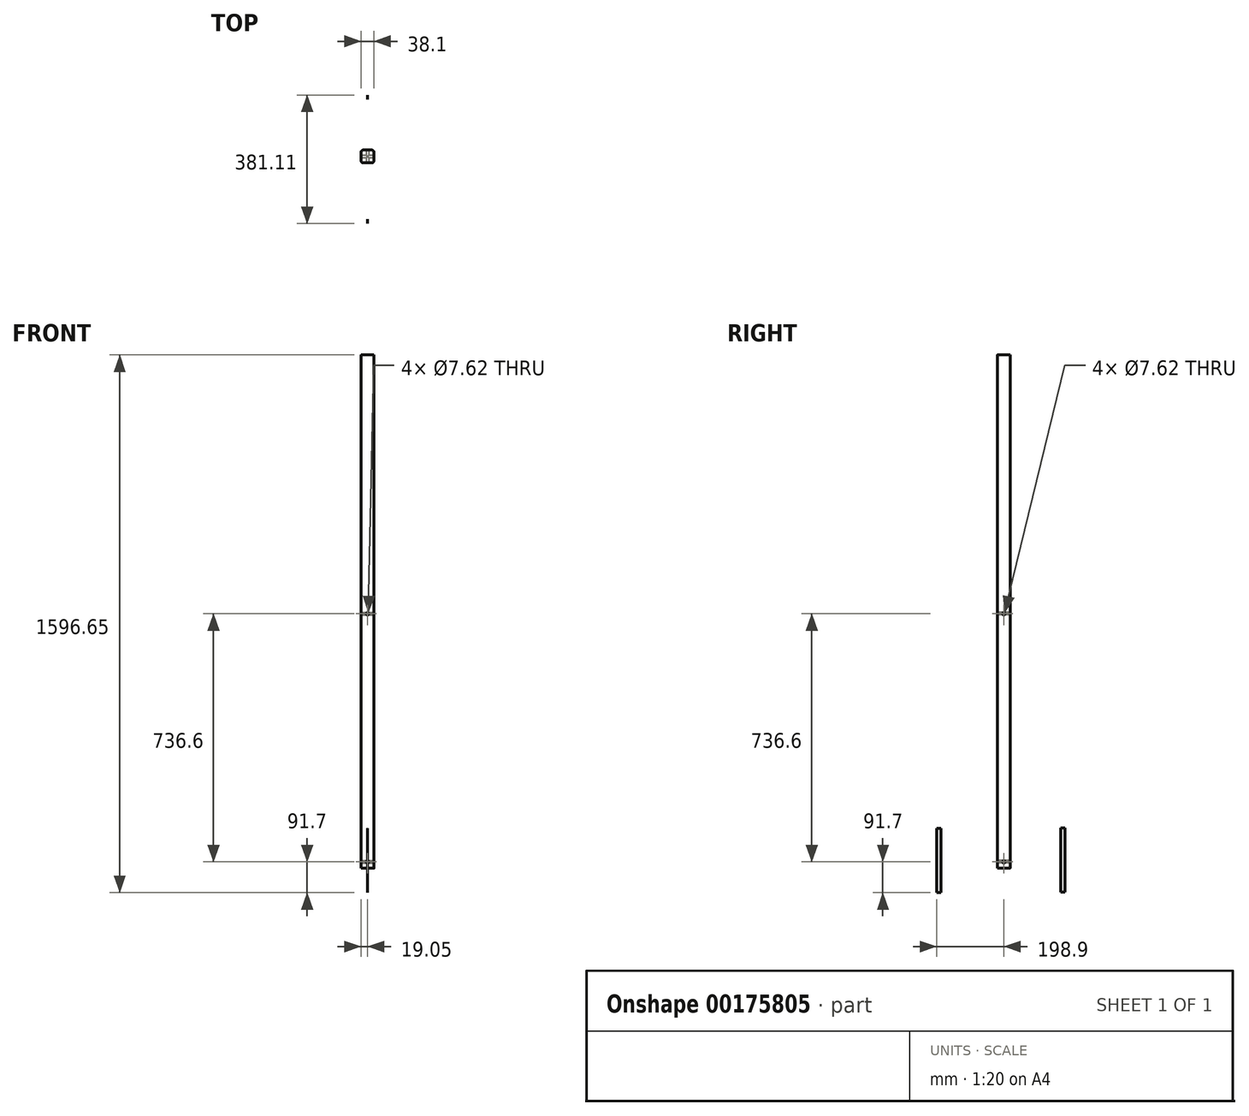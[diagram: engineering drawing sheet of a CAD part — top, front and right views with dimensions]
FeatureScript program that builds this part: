
annotation { "Feature Type Name" : "Feature", "Feature Type Description" : "" }
export const myFeature = defineFeature(function(context is Context, id is Id, definition is map)
    precondition{}
    {
        {
            var Q0;
            Q0=qCreatedBy(makeId("Top.planeOp"),FACE);
            var sketch = newSketch(context, id + "F0", { "sketchPlane" : qUnion([Q0])});
            skLineSegment(sketch, "E0.bottom", {"start": v(12.7, 19.05) * mm, "end": v(-12.7, 19.05) * mm});
            skLineSegment(sketch, "E0.top", {"start": v(12.7, -19.05) * mm, "end": v(-12.7, -19.05) * mm});
            skLineSegment(sketch, "E0.left", {"start": v(19.05, 12.7) * mm, "end": v(19.05, -12.7) * mm});
            skLineSegment(sketch, "E0.right", {"start": v(-19.05, 12.7) * mm, "end": v(-19.05, -12.7) * mm});
            skPoint(sketch, "E0.middle", {"position": v(0, 0) * mm});
            skPoint(sketch, "E1.visualSharp", {"position": v(-19.05, 19.05) * mm});
            skArc(sketch, "E1.filletArc", {"start": v(-12.7, 19.05) * mm, "mid": v(-17.2, 17.2) * mm, "end": v(-19.05, 12.7) * mm});
            skPoint(sketch, "E2.visualSharp", {"position": v(19.05, 19.05) * mm});
            skArc(sketch, "E2.filletArc", {"start": v(19.05, 12.7) * mm, "mid": v(17.2, 17.2) * mm, "end": v(12.7, 19.05) * mm});
            skPoint(sketch, "E3.visualSharp", {"position": v(19.05, -19.05) * mm});
            skArc(sketch, "E3.filletArc", {"start": v(12.7, -19.05) * mm, "mid": v(17.2, -17.2) * mm, "end": v(19.05, -12.7) * mm});
            skPoint(sketch, "E4.visualSharp", {"position": v(-19.05, -19.05) * mm});
            skArc(sketch, "E4.filletArc", {"start": v(-19.05, -12.7) * mm, "mid": v(-17.2, -17.2) * mm, "end": v(-12.7, -19.05) * mm});
            skSolve(sketch);
        }
        {
            var Q0;
            Q0=qSketchRegion(id+"F0",true);
            extrude(context, id + "F1", {"entities" : qUnion([Q0]), "depth" : 1524 * mm});
        }
        {
            var Q0;
            Q0=qCreatedBy(makeId("Right.planeOp"),FACE);
            var sketch = newSketch(context, id + "F2", { "sketchPlane" : qUnion([Q0])});
            skLineSegment(sketch, "E5.bottom", {"start": v(-186.2, -72.65) * mm, "end": v(-198.9, -72.65) * mm});
            skLineSegment(sketch, "E5.top", {"start": v(-186.2, 117.85) * mm, "end": v(-198.9, 117.85) * mm});
            skLineSegment(sketch, "E5.left", {"start": v(-186.2, -72.65) * mm, "end": v(-186.2, 117.85) * mm});
            skLineSegment(sketch, "E5.right", {"start": v(-198.9, -72.65) * mm, "end": v(-198.9, 117.85) * mm});
            skPoint(sketch, "E5.middle", {"position": v(-192.55, 22.6) * mm});
            skSolve(sketch);
        }
        {
            var Q0;
            Q0=qCreatedBy(makeId("Right.planeOp"),FACE);
            var sketch = newSketch(context, id + "F3", { "sketchPlane" : qUnion([Q0])});
            skLineSegment(sketch, "E6.bottom", {"start": v(182.21, -70.47) * mm, "end": v(169.51, -70.47) * mm});
            skLineSegment(sketch, "E6.top", {"start": v(182.21, 120.03) * mm, "end": v(169.51, 120.03) * mm});
            skLineSegment(sketch, "E6.left", {"start": v(182.21, -70.47) * mm, "end": v(182.21, 120.03) * mm});
            skLineSegment(sketch, "E6.right", {"start": v(169.51, -70.47) * mm, "end": v(169.51, 120.03) * mm});
            skPoint(sketch, "E6.middle", {"position": v(175.86, 24.78) * mm});
            skSolve(sketch);
        }
        {
            var Q0;
            Q0=makeQuery(id+"F2.imprint","IMPRINT",FACE,{"disambiguationData":[TD([[makeQuery(id+"F2.imprint","IMPRINT",EDGE,{"derivedFrom":sQuery(id+"F2.wireOp",EDGE,"E5.bottom")}),-1.0]])]});
            extrude(context, id + "F4", {"entities" : qUnion([Q0]), "depth" : 0.25 * mm});
        }
        {
            var Q0;
            Q0=makeQuery(id+"F3.imprint","IMPRINT",FACE,{"disambiguationData":[TD([[makeQuery(id+"F3.imprint","IMPRINT",EDGE,{"derivedFrom":sQuery(id+"F3.wireOp",EDGE,"E6.bottom")}),-1.0]])]});
            extrude(context, id + "F5", {"entities" : qUnion([Q0]), "depth" : 0.25 * mm});
        }
        {
            var Q0;
            Q0=makeQuery(id+"F1.opExtrude","SWEPT_FACE",FACE,{"disambiguationData":[OSD([sQuery(id+"F0.wireOp",EDGE,"E0.left")])]});
            var sketch = newSketch(context, id + "F6", { "sketchPlane" : qUnion([Q0])});
            skLineSegment(sketch, "E7", {"start": v(0, 0) * mm, "end": v(0, 755.65) * mm});
            skCircle(sketch, "E8", {"center": v(0, 755.65) * mm, "radius": 3.81 * mm});
            skSolve(sketch);
        }
        {
            var Q0;
            Q0 = qSketchRegion(id + "F6", true);
            extrude(context, id + "F7", {"entities" : qUnion([Q0]), "operationType" : NewBodyOperationType.REMOVE, "oppositeDirection" : true, "depth" : 38.1 * mm});
        }
        {
            var Q0;
            Q0=makeQuery(id+"F1.opExtrude","SWEPT_FACE",FACE,{"disambiguationData":[OSD([sQuery(id+"F0.wireOp",EDGE,"E0.top")])]});
            var sketch = newSketch(context, id + "F8", { "sketchPlane" : qUnion([Q0])});
            skLineSegment(sketch, "E9", {"start": v(0, 0) * mm, "end": v(0, 755.65) * mm});
            skCircle(sketch, "E10", {"center": v(0, 755.65) * mm, "radius": 3.81 * mm});
            skLineSegment(sketch, "E11", {"start": v(0, 0) * mm, "end": v(0, 19.05) * mm});
            skCircle(sketch, "E12", {"center": v(0, 19.05) * mm, "radius": 3.81 * mm});
            skSolve(sketch);
        }
        {
            var Q0;
            Q0 = qSketchRegion(id + "F8", true);
            extrude(context, id + "F9", {"entities" : qUnion([Q0]), "operationType" : NewBodyOperationType.REMOVE, "oppositeDirection" : true, "depth" : 38.1 * mm});
        }
        {
            var Q0;
            Q0 = qSketchRegion(id + "F8", true);
            extrude(context, id + "F10", {"entities" : qUnion([Q0]), "operationType" : NewBodyOperationType.REMOVE, "oppositeDirection" : true, "depth" : 38.1 * mm});
        }
        {
            var Q0;
            Q0=makeQuery(id+"F1.opExtrude","SWEPT_FACE",FACE,{"disambiguationData":[OSD([sQuery(id+"F0.wireOp",EDGE,"E0.left")])]});
            var sketch = newSketch(context, id + "F11", { "sketchPlane" : qUnion([Q0])});
            skLineSegment(sketch, "E13", {"start": v(0, 0) * mm, "end": v(0, 19.05) * mm});
            skPoint(sketch, "E13.endSnap0", {"position": v(0, 0) * mm});
            skCircle(sketch, "E14", {"center": v(0, 19.05) * mm, "radius": 3.81 * mm});
            skSolve(sketch);
        }
        {
            var Q0;
            Q0 = qSketchRegion(id + "F11", true);
            extrude(context, id + "F12", {"entities" : qUnion([Q0]), "operationType" : NewBodyOperationType.REMOVE, "oppositeDirection" : true, "depth" : 38.1 * mm});
        }
    });
